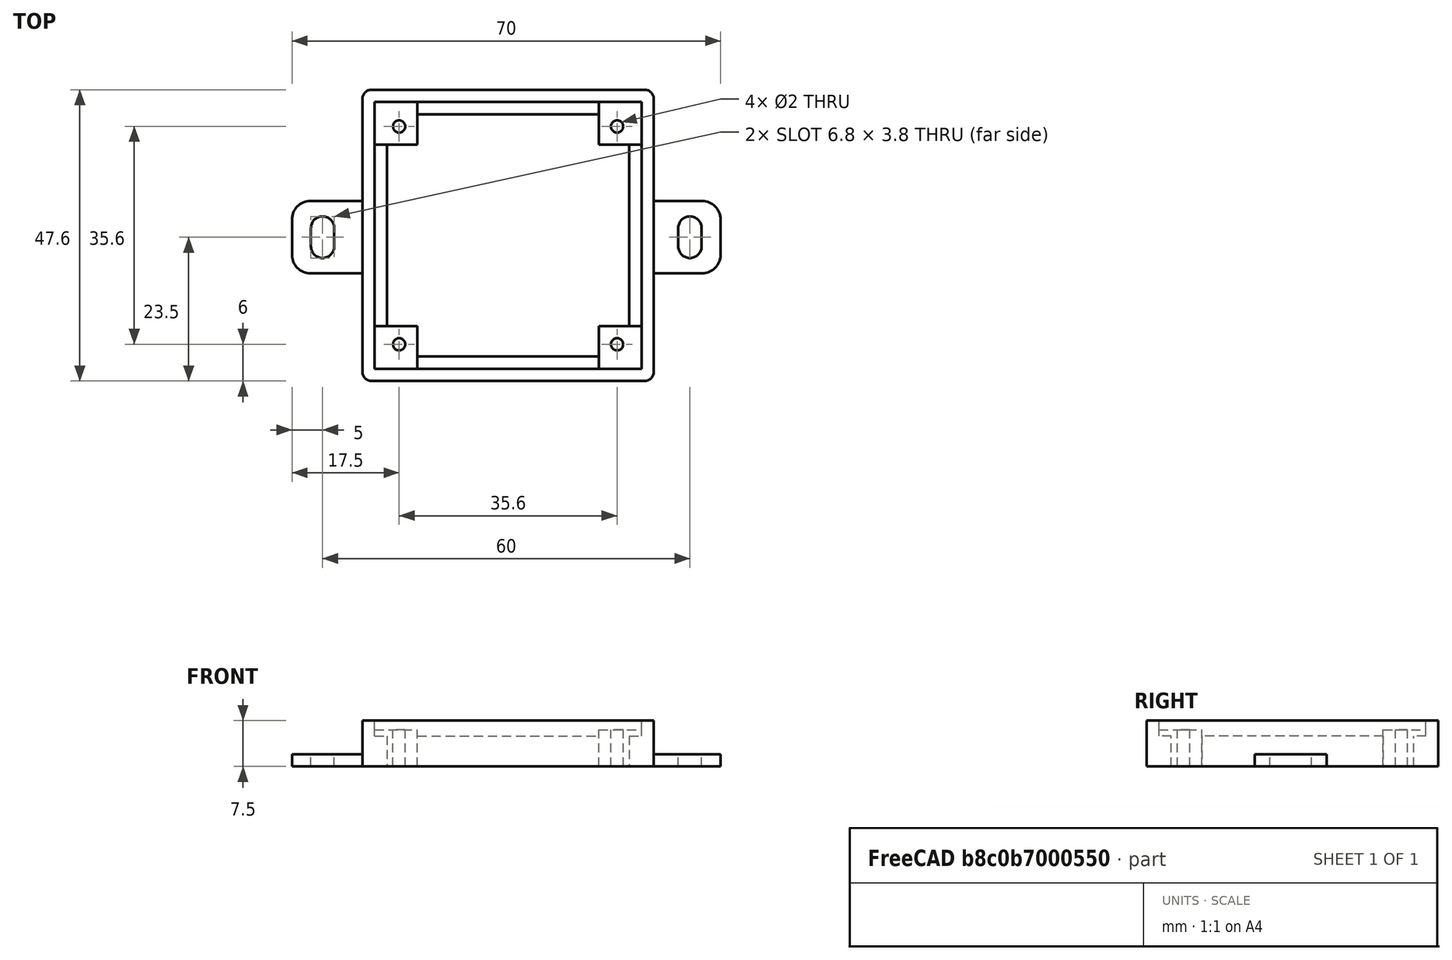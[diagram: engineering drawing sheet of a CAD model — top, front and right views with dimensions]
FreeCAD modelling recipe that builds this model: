
FCSTD DOCUMENT  (FreeCAD 0.19R23578 (Git))
Label: stepper_driver
License: All rights reserved
LicenseURL: http://en.wikipedia.org/wiki/All_rights_reserved
objects: Part::Box×4, Part::MultiFuse×3, Part::FeaturePython×2, Part::Cut×2, Spreadsheet::Sheet×1, Part::Cylinder×1, Part::Fillet×1, Part::Feature×1, App::Part×1
note: 14 computed .brp shape members not serialized (recipe doc carries the construction recipe); baked Part::Feature solids carry a one-line shape summary decoded from their .brp

FEATURE [Spreadsheet::Sheet] Spreadsheet  label="p"
  cells = A1=hole_x_dist; B1(hole_x_dist)=35.6; A2=hole_y_dist; B2(hole_y_dist)=35.6; A3=pcb_under; B3(pcb_under)=3; A4=pcb_x; B4(pcb_x)=43.6; A5=pcb_y; B5(pcb_y)=43.6; A6=hole_stand_x; B6(hole_stand_x)=7; A7=hole_stand_y; B7(hole_stand_y)=7; A8=hole_r; B8(hole_r)=1; A9=box_wall; B9(box_wall)=2; A10=under_layer; B10(under_layer)=3; A11=pcb_height; B11(pcb_height)=1.5; A12=under_pcb_border; B12(under_pcb_border)=2
FEATURE [Part::Box] Box  label="bottom cube"
  AttacherType = Attacher::AttachEngine3D
  Height = 7.5
  Length = 47.6
  Width = 47.6
  expr: Width = <<p>>.pcb_y + <<p>>.box_wall * 2
  expr: Length = <<p>>.pcb_x + <<p>>.box_wall * 2
  expr: Height = <<p>>.pcb_under + <<p>>.pcb_height + <<p>>.under_layer
FEATURE [Part::Box] Box001  label="bottom extraction"
  AttacherType = Attacher::AttachEngine3D
  Height = 10
  Length = 39.6
  Placement = pos=(4,4,0) rot=(0,0,1;0rad)
  Width = 39.6
  expr: .Placement.Base.y = <<p>>.under_pcb_border + <<p>>.box_wall
  expr: .Placement.Base.x = <<p>>.under_pcb_border + <<p>>.box_wall
  expr: Length = <<p>>.pcb_x - <<p>>.under_pcb_border * 2
  expr: Width = <<p>>.pcb_y - <<p>>.under_pcb_border * 2
FEATURE [Part::Box] Box002  label="pcb extraction"
  AttacherType = Attacher::AttachEngine3D
  Height = 10
  Length = 43.6
  Placement = pos=(2,2,5) rot=(0,0,1;0rad)
  Width = 43.6
  expr: .Placement.Base.z = <<p>>.under_pcb_border + <<p>>.under_layer
  expr: .Placement.Base.y = <<p>>.box_wall
  expr: .Placement.Base.x = <<p>>.box_wall
  expr: Length = <<p>>.pcb_x
  expr: Width = <<p>>.pcb_y
FEATURE [Part::MultiFuse] Fusion  label="bottom extraction001"
  Shapes = -> [Box001,Box002]
FEATURE [Part::Box] Box003  label="hole stand cube"
  AttacherType = Attacher::AttachEngine3D
  Height = 6
  Length = 7
  Placement = pos=(2,2,0) rot=(0,0,1;0rad)
  Width = 7
  expr: .Placement.Base.y = <<p>>.box_wall
  expr: .Placement.Base.x = <<p>>.box_wall
  expr: Height = <<p>>.pcb_under + <<p>>.under_layer
  expr: Width = <<p>>.hole_stand_y
  expr: Length = <<p>>.hole_stand_x
FEATURE [Part::FeaturePython] Array  label="hole stand array"  # Draft array (typed FeaturePython)
  Angle = 360
  ArrayType = 0
  Axis = (0,0,1)
  Base = -> Box003
  Center = (0,0,0)
  Fuse = false
  IntervalAxis = (0,0,0)
  IntervalX = (36.6,0,0)
  IntervalY = (0,36.6,0)
  IntervalZ = (0,0,1)
  NumberPolar = 1
  NumberX = 2
  NumberY = 2
  NumberZ = 1
  expr: .IntervalY.y = <<p>>.pcb_y - <<p>>.hole_stand_y
  expr: .IntervalX.x = <<p>>.pcb_x - <<p>>.hole_stand_x
FEATURE [Part::Cylinder] Cylinder  label="pcb hole"
  Angle = 360
  AttacherType = Attacher::AttachEngine3D
  Height = 10
  Placement = pos=(6,6,0) rot=(0,0,1;0rad)
  Radius = 1
  expr: .Placement.Base.y = (<<p>>.box_wall * 2 + <<p>>.pcb_y - <<p>>.hole_y_dist) / 2
  expr: .Placement.Base.x = (<<p>>.box_wall * 2 + <<p>>.pcb_x - <<p>>.hole_x_dist) / 2
  expr: Radius = <<p>>.hole_r
FEATURE [Part::FeaturePython] Array001  label="hole array"  # Draft array (typed FeaturePython)
  Angle = 360
  ArrayType = 0
  Axis = (0,0,1)
  Base = -> Cylinder
  Center = (0,0,0)
  Fuse = false
  IntervalAxis = (0,0,0)
  IntervalX = (35.6,0,0)
  IntervalY = (0,35.6,0)
  IntervalZ = (0,0,1)
  NumberPolar = 1
  NumberX = 2
  NumberY = 2
  NumberZ = 1
  expr: .IntervalY.y = <<p>>.hole_y_dist
  expr: .IntervalX.x = <<p>>.hole_x_dist
FEATURE [Part::Fillet] Fillet001  label="bottom cube fillet"
  Base = -> Box
  Edges = 4 edges r=1.5: [Edge1,Edge3,Edge5,Edge7]
FEATURE [Part::Feature] Cut003001  label="attach plane x dir001"
  Placement = pos=(-11.5,17.6,0) rot=(0,0,1;0rad)
  shape: bbox 70 x 11.8 x 2 mm, 18 faces (baked)
FEATURE [Part::MultiFuse] Fusion002  label="bottom fusion"
  Shapes = -> [Fillet001,Cut003001]
FEATURE [Part::Cut] Cut  label="pcb box cut"
  Base = -> Fusion002
  Tool = -> Fusion
FEATURE [Part::MultiFuse] Fusion001  label="frame fusion"
  Shapes = -> [Array,Cut]
FEATURE [Part::Cut] Cut001  label="frame fusion with holes"
  Base = -> Fusion001
  Tool = -> Array001
FEATURE [App::Part] Part  label="pcb with 4 holes part"
  Group = -> [Fusion,Fusion002,Box002,Box003,Box001,Array001,Box,Cut,Array,Cylinder,Fusion001,Cut001]
  Origin = -> Origin
